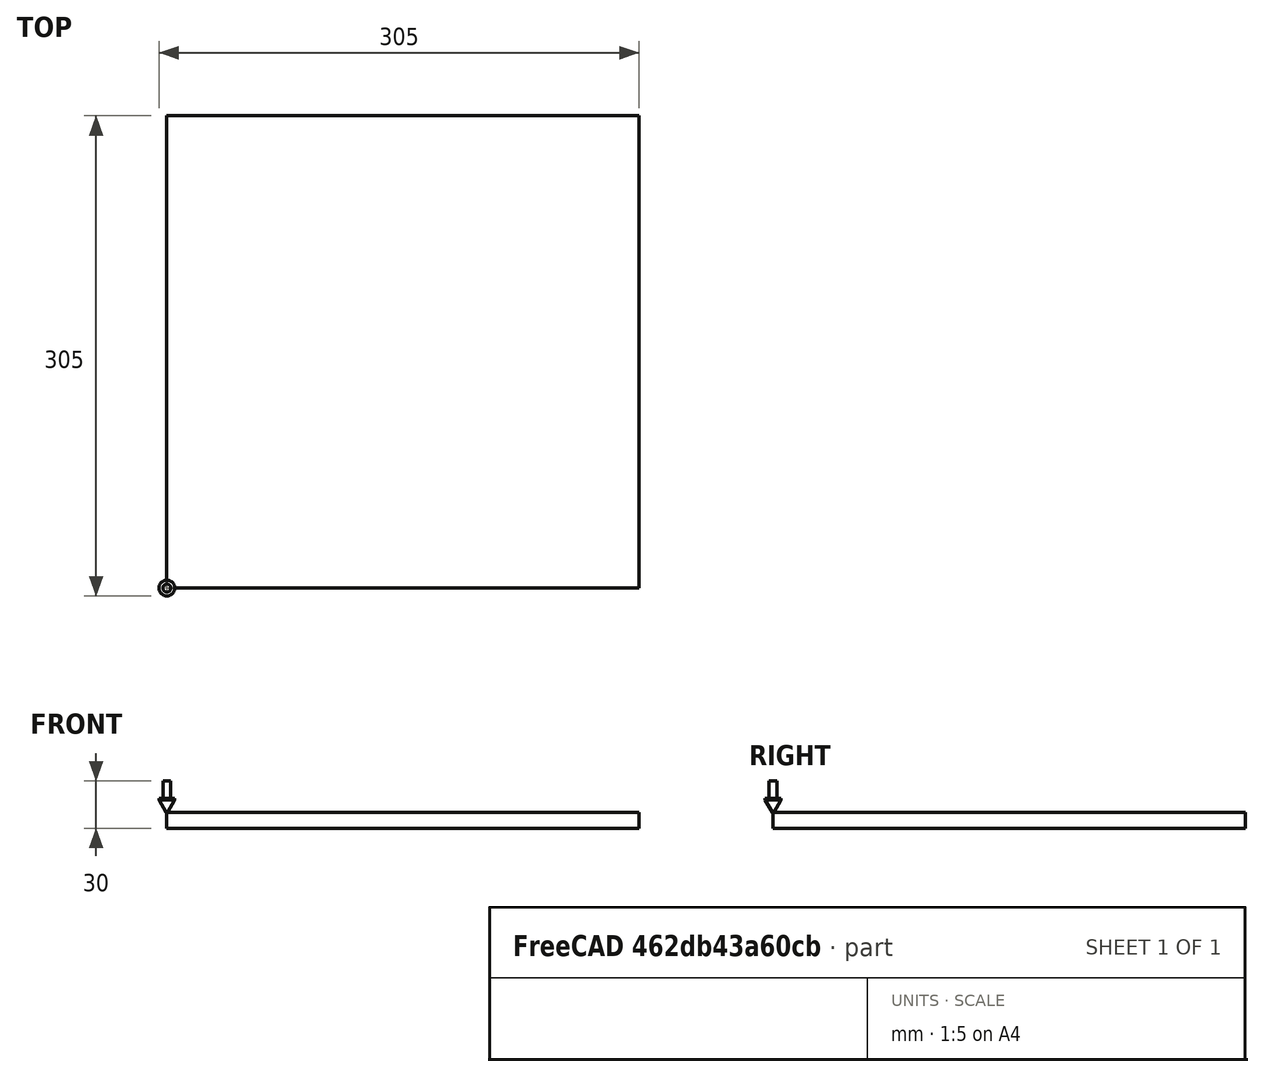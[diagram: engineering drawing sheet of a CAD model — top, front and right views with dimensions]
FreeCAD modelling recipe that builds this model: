
FCSTD DOCUMENT  (FreeCAD 0.19R14555 (Git shallow))
Label: testchamfer
License: All rights reserved
LicenseURL: http://en.wikipedia.org/wiki/All_rights_reserved
objects: Part::FeaturePython×3, Path::FeaturePython×3, App::DocumentObjectGroup×2, Mesh::FeaturePython×2, Sketcher::SketchObject×1, PartDesign::Pad×1, PartDesign::Chamfer×1, PartDesign::Body×1, App::FeaturePython×1, Path::FeatureCompoundPython×1
note: 10 computed .brp shape members not serialized (recipe doc carries the construction recipe); baked Part::Feature solids carry a one-line shape summary decoded from their .brp

FEATURE [Sketcher::SketchObject] Sketch
  FullyConstrained = true
  MapMode = 5
  Support = -> [XY_Plane]
  sketch-geometry (5):
    g0: LineSegment StartX=0 StartY=300 StartZ=0 EndX=300 EndY=300 EndZ=0
    g1: LineSegment StartX=300 StartY=300 StartZ=0 EndX=300 EndY=0 EndZ=0
    g2: LineSegment StartX=300 StartY=0 StartZ=0 EndX=0 EndY=0 EndZ=0
    g3: LineSegment StartX=0 StartY=0 StartZ=0 EndX=0 EndY=300 EndZ=0
    g4: Circle CenterX=150 CenterY=150 CenterZ=0 NormalX=0 NormalY=0 NormalZ=1 AngleXU=0 Radius=75
  constraints (14):
    c: Coincident(g0,g1)
    c: Coincident(g1,g2)
    c: Coincident(g2,g3)
    c: Coincident(g3,g0)
    c: Horizontal(g0)
    c: Horizontal(g2)
    c: Vertical(g1)
    c: Vertical(g3)
    c: Coincident(g2,g-1)
    c: DistanceX(g2,g1) = 300
    c: DistanceY(g2,g0) = 300
    c: DistanceX(g2,g4) = 150
    c: DistanceY(g2,g4) = 150
    c: Diameter(g4) = 150
FEATURE [PartDesign::Pad] Pad
  Direction = (1,1,1)
  Length = 10
  Length2 = 100
  Profile = -> Sketch
  Reversed = true
  Type = 0
FEATURE [PartDesign::Chamfer] Chamfer
  Angle = 45
  Base = -> Pad [Edge14]
  BaseFeature = -> Pad
  ChamferType = 0
  FlipDirection = false
  Size = 6
  Size2 = 1
  SupportTransform = false
FEATURE [PartDesign::Body] Body
  Group = -> [Sketch,Pad,Chamfer]
  Origin = -> Origin
  Tip = -> Chamfer
FEATURE [App::FeaturePython] SetupSheet  # Path/CAM operation (typed FeaturePython)
  ClearanceHeightExpression = OpStockZMax+SetupSheet.ClearanceHeightOffset
  ClearanceHeightOffset = 5
  CoolantMode = 0
  CoolantModes = None | Flood | Mist
  FinalDepthExpression = OpFinalDepth
  HorizRapid = 0
  SafeHeightExpression = OpStockZMax+SetupSheet.SafeHeightOffset
  SafeHeightOffset = 3
  StartDepthExpression = OpStartDepth
  StepDownExpression = OpToolDiameter
  VertRapid = 0
FEATURE [Part::FeaturePython] Clone  label="Model-Body"  # Draft clone (typed FeaturePython)
  AttacherType = Attacher::AttachEngine3D
  Fuse = false
  Objects = -> [Body]
  PathResource = Model
  Scale = (1,1,1)
FEATURE [App::DocumentObjectGroup] Model
  Group = -> [Clone]
FEATURE [Part::FeaturePython] ToolBit001  label="60 Deg. V-Bit"  # Path/CAM toolbit (typed FeaturePython)
  BitPropertyNames = Chipload | CuttingEdgeAngle | CuttingEdgeHeight | Diameter | Flutes | Length | Material | ShankDiameter | TipDiameter
  BitShape = /app/freecad/Mod/Path/Tools/Shape/v-bit.fcstd
  Chipload = 0
  CuttingEdgeAngle = 60
  CuttingEdgeHeight = 1
  Diameter = 10
  File = <userpath>/Documents/MensShed/FreeCAD/Bit/60degree_Vbit.fctb
  Flutes = 0
  Length = 20
  Material = 0
  ShankDiameter = 5
  ShapeName = v_bit
  TipDiameter = 1
FEATURE [Path::FeaturePython] _0_Deg__V_Bit  label="60 Deg. V-Bit001"  # Path/CAM operation (typed FeaturePython)
  HorizFeed = 20
  HorizRapid = 0
  SpindleDir = 0
  SpindleSpeed = 10000
  Tool = -> ToolBit001
  ToolNumber = 2
  VertFeed = 20
  VertRapid = 0
  expr: HorizRapid = SetupSheet.HorizRapid
  expr: VertRapid = SetupSheet.VertRapid
FEATURE [App::DocumentObjectGroup] Tools
  Group = -> [_0_Deg__V_Bit]
FEATURE [Part::FeaturePython] Stock001  # WARN: FeaturePython — macro-defined, semantics opaque (R4)
  Height = 10
  Length = 300
  Placement = pos=(0,0,-10) rot=(0,0,1;0rad)
  StockType = CreateBox
  Width = 300
FEATURE [Path::FeaturePython] Profile  # Path/CAM operation (typed FeaturePython)
  Active = true
  AreaParams:
    Tolerance = 1e-07
    FitArcs = True
    Simplify = False
    CleanDistance = 0.0
    Accuracy = 0.01
    Unit = 1.0
    MinArcPoints = 4
    MaxArcPoints = 100
    ClipperScale = 10000000.0
    Fill = 0
    Coplanar = 0
    Reorient = True
    Outline = False
    Explode = False
    OpenMode = 0
    Deflection = 0.01
    SubjectFill = 0
    ClipFill = 0
    Offset = -5.0
    ExtraPass = 0
    Stepover = 0.0
    LastStepover = 0.0
    JoinType = 0
    EndType = 0
    MiterLimit = 2.0
    RoundPrecision = 0.0
    PocketMode = 0
    ToolRadius = 1.0
    PocketExtraOffset = 0.0
    PocketStepover = 0.0
    PocketLastStepover = 0.0
    FromCenter = False
    Angle = 45.0
    AngleShift = 0.0
    Shift = 0.0
    Thicken = False
    SectionCount = -1
    Stepdown = 1.0
    SectionOffset = 0.0
    SectionTolerance = 1e-06
    SectionMode = 2
    Project = False
  AttemptInverseAngle = true
  Base = -> [Clone]
  ClearanceHeight = 5
  CoolantMode = None
  CycleTime = 00:00:31
  Direction = 0
  EnableRotation = 0
  FinalDepth = -6
  HandleMultipleFeatures = 0
  InverseAngle = false
  JoinType = 0
  LimitDepthToFace = true
  MiterLimit = 0.1
  OffsetExtra = 0
  OpFinalDepth = -6
  OpStartDepth = 0
  OpStockZMax = 0
  OpStockZMin = -10
  OpToolDiameter = 10
  PathParams = {'orientation': 1, 'feedrate': 20.0, 'feedrate_v': 20.0, 'verbose': True, 'resume_height': 3.0, 'retraction': 5.0, 'return_end': True, 'preamble': False}
  ReverseDirection = false
  SafeHeight = 3
  Side = 1
  StartDepth = 0
  StartPoint = (0,0,0)
  StepDown = 10
  ToolController = -> _0_Deg__V_Bit
  UseComp = true
  UseStartPoint = false
  processCircles = false
  processHoles = false
  processPerimeter = true
  expr: ClearanceHeight = OpStockZMax + SetupSheet.ClearanceHeightOffset
  expr: SafeHeight = OpStockZMax + SetupSheet.SafeHeightOffset
  expr: StepDown = OpToolDiameter
  expr: FinalDepth = OpFinalDepth
  expr: StartDepth = OpStartDepth
FEATURE [Path::FeatureCompoundPython] Operations  # Path/CAM operation (typed FeaturePython)
  Group = -> [Profile]
  UsePlacements = false
FEATURE [Path::FeaturePython] Job  # Path/CAM operation (typed FeaturePython)
  CycleTime = 00:00:31
  Fixtures = G54
  GeometryTolerance = 0.01
  LastPostProcessDate = 2022-01-20 10:28:37.105215
  LastPostProcessOutput = <userpath>/Documents/MensShed/testchamfer.ngc
  Model = -> Model
  Operations = -> Operations
  OrderOutputBy = 0
  PostProcessor = 7
  PostProcessorOutputFile = <userpath>/Documents/MensShed/testchamfer.ngc
  SetupSheet = -> SetupSheet
  SplitOutput = false
  Stock = -> Stock001
  Tools = -> Tools
FEATURE [Mesh::FeaturePython] CutMaterial  # WARN: FeaturePython — macro-defined, semantics opaque (R4)
FEATURE [Mesh::FeaturePython] CutMaterial001  # WARN: FeaturePython — macro-defined, semantics opaque (R4)
